# Revit family: P550069-020
name_source: partatom
category: Lighting Fixtures
revit_build: Autodesk Revit 2014 (Build: 20130308_1515(x64)
units: mm (PartAtom-declared; Revit-internal decimal feet)

## types (1)
- P550069-020
    Apparent Load = 60 VA
    Assembly Code = D5020200
    Connector Description = Lighting Connector
    Default Elevation = 48 "
    Description = Barlowe Collection Two-Light Antique Bronze and Clear Seeded Glass Farmhouse Style Flush Mount Ceiling Light
    Fab = soft brass
    Features = Application: Transform your home into a warm and cozy retreat with the Barlowe Collection 2-Light Antique Bronze Clear Seeded Glass Farmhouse Outdoor Flush Mount Ceiling Light ideal for any hallway, stairwell, entryway, kitchen, sitting room, covered porch, or patio.
Styles: Perfect for farmhouse, coastal, and transitional style settings.
Finish: A rustic cross-brace design decorates the charming square silhouette coated in a handsome antique bronze finish.
Materials: Constructed from steel to ensure a long product lifespan.
Glass/Shades: Light sources glow through clear seeded glass panes add an extra pop of rustic personality.
Bulbs: For ideal illumination, use 2 medium base bulbs that are sold separately (60w max - LED/CFL/incandescent). Compatible with dimmable bulbs.
Dimensions: Measures 11-inch length by 11-1/2-inch width by 5-1/2-inch height.
Certifications: cCSAus damp location listed.
Pairs With: Pairs with a variety of Progress Lighting fixtures.
Warranty: Our 1-Year Limited Warranty guarantees your complete satisfaction with your purchase and includes professional after-sales customer service support.
    Fixture distribution = Direct
    Glass = Paint - Hubbell - White Texture
    Gold = Hubbell - Gold
    Housing Material = Hubbell Metal Brass
    Lamp = LED/CFL/incandescent
    Load Classification = Lighting
    Manufacturer = Progress Lighting
    Model = P550069-020
    Power Factor = 1
    Product Documentation Link = https://hubbellcdn.com
    Product Link = https://www.hubbell.com
    Support = Paint - Hubbell - Light Silver
    URL = https://www.hubbell.com
    Voltage = 120 V
    Warranty = 1 year Warranty
    Wattage Comments = 60W
    Watts = 60 W

## geometry (parser evidence)
native form markers: Sweep x5
no freeform markers — native parametric forms only
